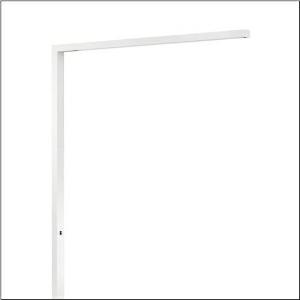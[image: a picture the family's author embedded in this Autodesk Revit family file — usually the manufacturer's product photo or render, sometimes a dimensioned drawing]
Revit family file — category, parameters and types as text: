
# Revit family: silica_r__11_floor_5mx51bs3wzk00002xx_06fb
name_source: partatom
category: Lighting Fixtures
units: mm (PartAtom-declared; Revit-internal decimal feet)

## family parameters
Cut with Voids When Loaded = No
Host = Face
Light Source = No
Part Type = Normal
Room Calculation Point = No
Round Connector Dimension = Use Diameter
Shared = No

## types (1)
- --- (1 x LED, 3960 lm / 8500 lm, 24.4 W / 54.9 W, 4000K)
    Apparent Load = 79 VA
    CIE Flux Codes = 82 97 100 100 100 / - - - 0 100
    Color Rendering = 80
    Color Temperature = 4000K
    Default Elevation = 1800 mm
    Description = Silica® 11 Floor, floorstanding luminaire, of PMMA, primary optical cover: cover panel, of PMMA, light emission: indirect/direct distribution, primary light characteristic: symmetric, installation type: not mounted, LED, rated luminous flux: 12.460lm, luminous efficacy: 157lm/W, light colour: 840, colour temperature: 4000K, control gear: DALI, daylight-dependent control, mains connection: 230V, AC, 50Hz, connection cable pre-assembled, cable length: 3m, rated input power: 79W, luminaire head, rectangular, rounded, of aluminium, coated, traffic white (RAL 9016), supporting column, angular, of aluminium, coated, traffic white (RAL 9016), baseplate, of steel, coated, traffic white (RAL 9016), length: 1.316mm, width: 65mm, protection rating (complete): IP20, insulation class (complete): insulation class I (protective earthing), certification: CE, permissible operating ambient temperature: 0..+35°C, standard: EN 50419, packaging unit: 1 piece
    Height = 40 mm  [stored 0.131234 ft]
    Lamp = 1 x LED
    Lamp Light Flux = 3960 lm / 8500 lm
    Lamp Power = 24.4 W / 54.9 W
    Lamp count = 1
    Length = 1317 mm
    Luminous efficacy = 157 lm/W
    Manufacturer = Siteco
    ModVariant = No
    Model = 5MX51BS3WZK00002XX
    Mounting Place = Floor
    Mounting Type = Freestanding
    Number of Poles = 1
    OnlyDefault = Yes
    Power Factor = 1
    Product Name = Silica® 11 Floor
    Product group = floorstanding luminaire
    ProductGroupID = 1302
    Protection Class = Protection class I
    Protection Degree = IP 20
    RLX_Detail_Level = 1
    RLX_Emergency_Light_Flux = 0 lm
    RLX_Emergency_Type = 0
    RLX_Emergency_Type_DB = No
    RlxData = <blob elided: 18221 chars, md5=63eb8ecd>
    Socket = socket
    Standby Power = 0 W
    System Light Flux = 12460 lm
    System Power = 79 W
    Type Comments = factory setting: direct and indirect light
    Type Image = l_1004655.jpg
    URL = http://relux.com
    VarID = @adj_219536
    Voltage = 0 V
    Weight = 0.00 kg
    Width = 65 mm

note: [stored X ft] marks values corroborated as IEEE doubles in the binary element streams (Revit-internal decimal feet)

## geometry (parser evidence)
native form markers: Blend x4, Sweep x16
no freeform markers — native parametric forms only
